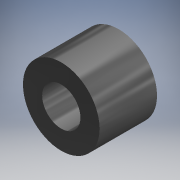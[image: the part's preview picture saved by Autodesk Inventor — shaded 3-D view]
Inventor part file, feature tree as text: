
AUTODESK INVENTOR PART (.ipt)
format: ipt  version: 2019 (Build 230136000, 136)  size: 90,112 bytes
history: native  units: mm (DEFAULTED — no unit token found)
features: extrude x1, sketch x1
ambient origin geometry x8: Origin, YZ Plane, XZ Plane, XY Plane, X Axis, Y Axis, Z Axis, Center Point
bodies: Solid1 (feature_tree)
feature tree (2):
  extrude  "Extrusion1"  Depth=9.525mm
  sketch  "Sketch1"  dims[d0=6.35mm d1=12.7mm d2=9.525mm d3=0.0mm]
